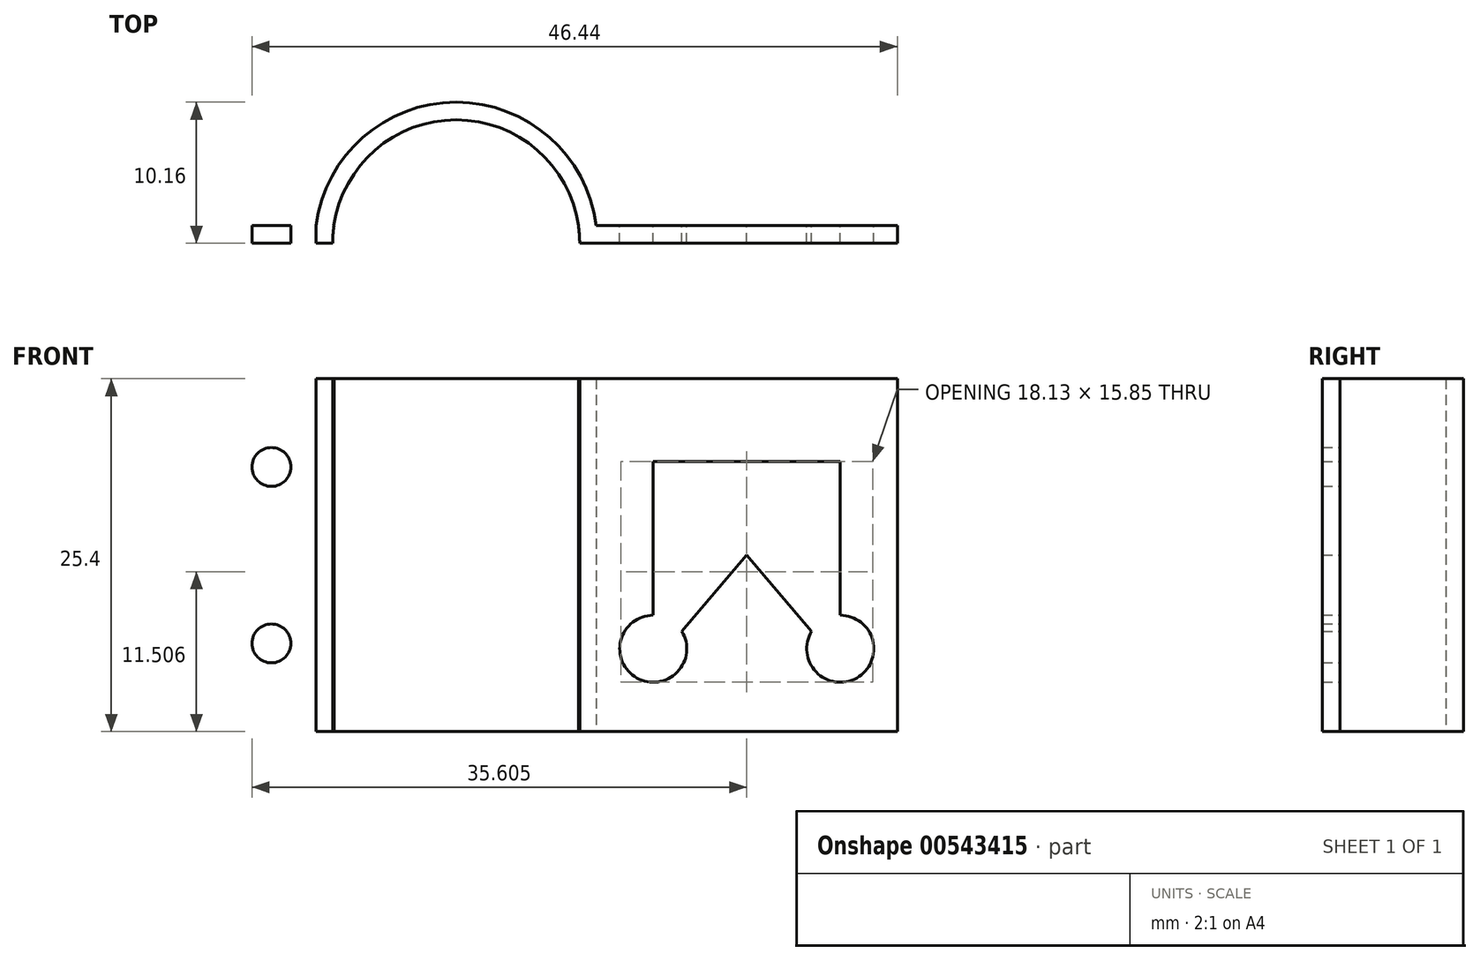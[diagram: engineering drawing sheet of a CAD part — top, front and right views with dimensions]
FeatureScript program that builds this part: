
annotation { "Feature Type Name" : "Feature", "Feature Type Description" : "" }
export const myFeature = defineFeature(function(context is Context, id is Id, definition is map)
    precondition{}
    {
        {
            var Q0;
            Q0=qCreatedBy(makeId("Top.planeOp"),FACE);
            var sketch = newSketch(context, id + "F0", { "sketchPlane" : qUnion([Q0])});
            skArc(sketch, "E0", {"start": v(8.8, 1.27) * mm, "mid": v(0, 8.9) * mm, "end": v(-8.8, 1.27) * mm});
            skArc(sketch, "E1", {"start": v(10.08, 1.27) * mm, "mid": v(0, 10.16) * mm, "end": v(-10.08, 1.27) * mm});
            skLineSegment(sketch, "E2", {"start": v(-10.16, 0) * mm, "end": v(-8.9, 0) * mm});
            skLineSegment(sketch, "E3.trimOffspring", {"start": v(8.9, 0) * mm, "end": v(10.16, 0) * mm});
            skLineSegment(sketch, "E4", {"start": v(-16.51, 0) * mm, "end": v(-8.89, 0) * mm});
            skLineSegment(sketch, "E5", {"start": v(-16.51, 1.27) * mm, "end": v(-10.08, 1.27) * mm});
            skLineSegment(sketch, "E6", {"start": v(-16.51, 1.27) * mm, "end": v(-16.51, 0) * mm});
            skLineSegment(sketch, "E7", {"start": v(31.75, 1.27) * mm, "end": v(31.75, 0) * mm});
            skPoint(sketch, "E8.start.orphan", {"position": v(-23.59, 0) * mm});
            skLineSegment(sketch, "E9.trimOffspring", {"start": v(-8.8, 1.27) * mm, "end": v(-8.8, 1.27) * mm});
            skLineSegment(sketch, "E10.trimOffspring", {"start": v(10.08, 1.27) * mm, "end": v(31.75, 1.27) * mm});
            skArc(sketch, "E11", {"start": v(8.9, 0) * mm, "mid": v(0, 8.86) * mm, "end": v(-8.9, 0) * mm});
            skLineSegment(sketch, "E12.trimOffspring", {"start": v(8.8, 1.27) * mm, "end": v(8.8, 1.27) * mm});
            skLineSegment(sketch, "E13.trimOffspring", {"start": v(8.9, 0) * mm, "end": v(31.75, 0) * mm});
            skSolve(sketch);
        }
        {
            var Q0;
            Q0=makeQuery(id+"F0.imprint","IMPRINT",FACE,{"disambiguationData":[TD([[makeQuery(id+"F0.imprint","IMPRINT",EDGE,{"derivedFrom":sQuery(id+"F0.wireOp",EDGE,"E0")}),-1.0]])]});
            extrude(context, id + "F1", {"entities" : qUnion([Q0]), "depth" : 25.4 * mm, "offsetDistance" : 25.4 * mm});
        }
        {
            var Q0;
            Q0=makeQuery(id+"F1.opExtrude","SWEPT_FACE",FACE,{"disambiguationData":[OSD([sQuery(id+"F0.wireOp",EDGE,"E5")])]});
            var sketch = newSketch(context, id + "F2", { "sketchPlane" : qUnion([Q0])});
            skLineSegment(sketch, "E14", {"start": v(13.3, 25.4) * mm, "end": v(13.3, 0) * mm});
            skPoint(sketch, "E15.orphan", {"position": v(10.08, 12.7) * mm});
            skPoint(sketch, "E16.orphan", {"position": v(16.51, 12.7) * mm});
            skCircle(sketch, "E17", {"center": v(13.3, 19.05) * mm, "radius": 1.4 * mm});
            skCircle(sketch, "E18", {"center": v(13.3, 12.7) * mm, "radius": 1.4 * mm});
            skCircle(sketch, "E19", {"center": v(13.3, 6.35) * mm, "radius": 1.4 * mm});
            skSolve(sketch);
        }
        {
            var Q0;
            Q0=makeQuery(id+"F1.opExtrude","SWEPT_FACE",FACE,{"disambiguationData":[OSD([sQuery(id+"F0.wireOp",EDGE,"E10.trimOffspring")])]});
            var sketch = newSketch(context, id + "F3", { "sketchPlane" : qUnion([Q0])});
            skLineSegment(sketch, "E20", {"start": v(-31.75, 25.4) * mm, "end": v(-10.08, 0) * mm});
            skLineSegment(sketch, "E21", {"start": v(-10.08, 25.4) * mm, "end": v(-31.75, 0) * mm});
            skLineSegment(sketch, "E22.bottom", {"start": v(-14.18, 19.43) * mm, "end": v(-27.65, 19.43) * mm});
            skLineSegment(sketch, "E22.top", {"start": v(-14.18, 5.97) * mm, "end": v(-27.65, 5.97) * mm});
            skLineSegment(sketch, "E22.left", {"start": v(-14.18, 19.43) * mm, "end": v(-14.18, 5.97) * mm});
            skLineSegment(sketch, "E22.right", {"start": v(-27.65, 19.43) * mm, "end": v(-27.65, 5.97) * mm});
            skPoint(sketch, "E22.middle", {"position": v(-20.92, 12.7) * mm});
            skCircle(sketch, "E23", {"center": v(-27.65, 19.43) * mm, "radius": 2.41 * mm});
            skCircle(sketch, "E24", {"center": v(-14.18, 19.43) * mm, "radius": 2.41 * mm});
            skCircle(sketch, "E25", {"center": v(-27.65, 5.97) * mm, "radius": 2.41 * mm});
            skCircle(sketch, "E26", {"center": v(-14.18, 5.97) * mm, "radius": 2.41 * mm});
            skSolve(sketch);
        }
        {
            var Q0;
            {var subQ0=sQuery(id+"F3.wireOp",EDGE,"E22.bottom");var subQ1=sQuery(id+"F3.wireOp",EDGE,"E20");var subQ2=makeQuery(id+"F3.imprint","INTERSECT",VERTEX,{"derivedFrom":[subQ1,subQ0]});Q0=makeQuery(id+"F3.imprint","IMPRINT",FACE,{"disambiguationData":[TD([[makeQuery(id+"F3.imprint","IMPRINT",EDGE,{"disambiguationData":[TD([[subQ2,-1.0]])],"derivedFrom":subQ1}),-1.0]])]});}
            var Q1;
            {var subQ0=sQuery(id+"F3.wireOp",EDGE,"E22.bottom");var subQ1=sQuery(id+"F3.wireOp",EDGE,"E20");var subQ2=makeQuery(id+"F3.imprint","INTERSECT",VERTEX,{"derivedFrom":[subQ1,subQ0]});Q1=makeQuery(id+"F3.imprint","IMPRINT",FACE,{"disambiguationData":[TD([[makeQuery(id+"F3.imprint","IMPRINT",EDGE,{"disambiguationData":[TD([[subQ2,-1.0]])],"derivedFrom":subQ1}),1.0]])]});}
            var Q2;
            {var subQ0=sQuery(id+"F3.wireOp",EDGE,"E23");var subQ1=sQuery(id+"F3.wireOp",EDGE,"E20");var subQ2=makeQuery(id+"F3.imprint","INTERSECT",VERTEX,{"disambiguationData":[OD(0.0)],"derivedFrom":[subQ1,subQ0]});Q2=makeQuery(id+"F3.imprint","IMPRINT",FACE,{"disambiguationData":[TD([[makeQuery(id+"F3.imprint","IMPRINT",EDGE,{"disambiguationData":[TD([[subQ2,-1.0]])],"derivedFrom":subQ1}),1.0]])]});}
            var Q3;
            {var subQ0=sQuery(id+"F3.wireOp",EDGE,"E23");var subQ1=sQuery(id+"F3.wireOp",EDGE,"E20");var subQ2=makeQuery(id+"F3.imprint","INTERSECT",VERTEX,{"disambiguationData":[OD(0.0)],"derivedFrom":[subQ1,subQ0]});Q3=makeQuery(id+"F3.imprint","IMPRINT",FACE,{"disambiguationData":[TD([[makeQuery(id+"F3.imprint","IMPRINT",EDGE,{"disambiguationData":[TD([[subQ2,-1.0]])],"derivedFrom":subQ1}),-1.0]])]});}
            var Q4;
            {var subQ0=sQuery(id+"F3.wireOp",EDGE,"E22.top");var subQ1=sQuery(id+"F3.wireOp",EDGE,"E21");var subQ2=makeQuery(id+"F3.imprint","INTERSECT",VERTEX,{"derivedFrom":[subQ1,subQ0]});Q4=makeQuery(id+"F3.imprint","IMPRINT",FACE,{"disambiguationData":[TD([[makeQuery(id+"F3.imprint","IMPRINT",EDGE,{"disambiguationData":[TD([[subQ2,-1.0]])],"derivedFrom":subQ1}),-1.0]])]});}
            var Q5;
            {var subQ0=sQuery(id+"F3.wireOp",EDGE,"E22.top");var subQ1=sQuery(id+"F3.wireOp",EDGE,"E21");var subQ2=makeQuery(id+"F3.imprint","INTERSECT",VERTEX,{"derivedFrom":[subQ1,subQ0]});Q5=makeQuery(id+"F3.imprint","IMPRINT",FACE,{"disambiguationData":[TD([[makeQuery(id+"F3.imprint","IMPRINT",EDGE,{"disambiguationData":[TD([[subQ2,-1.0]])],"derivedFrom":subQ1}),1.0]])]});}
            var Q6;
            {var subQ0=sQuery(id+"F3.wireOp",EDGE,"E25");var subQ1=sQuery(id+"F3.wireOp",EDGE,"E21");var subQ2=makeQuery(id+"F3.imprint","INTERSECT",VERTEX,{"disambiguationData":[OD(0.0)],"derivedFrom":[subQ1,subQ0]});Q6=makeQuery(id+"F3.imprint","IMPRINT",FACE,{"disambiguationData":[TD([[makeQuery(id+"F3.imprint","IMPRINT",EDGE,{"disambiguationData":[TD([[subQ2,-1.0]])],"derivedFrom":subQ1}),1.0]])]});}
            var Q7;
            {var subQ0=sQuery(id+"F3.wireOp",EDGE,"E25");var subQ1=sQuery(id+"F3.wireOp",EDGE,"E21");var subQ2=makeQuery(id+"F3.imprint","INTERSECT",VERTEX,{"disambiguationData":[OD(0.0)],"derivedFrom":[subQ1,subQ0]});Q7=makeQuery(id+"F3.imprint","IMPRINT",FACE,{"disambiguationData":[TD([[makeQuery(id+"F3.imprint","IMPRINT",EDGE,{"disambiguationData":[TD([[subQ2,-1.0]])],"derivedFrom":subQ1}),-1.0]])]});}
            var Q8;
            {var subQ0=sQuery(id+"F3.wireOp",EDGE,"E26");var subQ1=sQuery(id+"F3.wireOp",EDGE,"E20");var subQ2=makeQuery(id+"F3.imprint","INTERSECT",VERTEX,{"disambiguationData":[OD(0.0)],"derivedFrom":[subQ1,subQ0]});Q8=makeQuery(id+"F3.imprint","IMPRINT",FACE,{"disambiguationData":[TD([[makeQuery(id+"F3.imprint","IMPRINT",EDGE,{"disambiguationData":[TD([[subQ2,-1.0]])],"derivedFrom":subQ1}),-1.0]])]});}
            var Q9;
            {var subQ0=sQuery(id+"F3.wireOp",EDGE,"E22.top");var subQ1=sQuery(id+"F3.wireOp",EDGE,"E20");var subQ2=makeQuery(id+"F3.imprint","INTERSECT",VERTEX,{"derivedFrom":[subQ1,subQ0]});Q9=makeQuery(id+"F3.imprint","IMPRINT",FACE,{"disambiguationData":[TD([[makeQuery(id+"F3.imprint","IMPRINT",EDGE,{"disambiguationData":[TD([[subQ2,-1.0]])],"derivedFrom":subQ1}),-1.0]])]});}
            var Q10;
            {var subQ0=sQuery(id+"F3.wireOp",EDGE,"E22.top");var subQ1=sQuery(id+"F3.wireOp",EDGE,"E20");var subQ2=makeQuery(id+"F3.imprint","INTERSECT",VERTEX,{"derivedFrom":[subQ1,subQ0]});Q10=makeQuery(id+"F3.imprint","IMPRINT",FACE,{"disambiguationData":[TD([[makeQuery(id+"F3.imprint","IMPRINT",EDGE,{"disambiguationData":[TD([[subQ2,-1.0]])],"derivedFrom":subQ1}),1.0]])]});}
            var Q11;
            {var subQ0=sQuery(id+"F3.wireOp",EDGE,"E26");var subQ1=sQuery(id+"F3.wireOp",EDGE,"E20");var subQ2=makeQuery(id+"F3.imprint","INTERSECT",VERTEX,{"disambiguationData":[OD(0.0)],"derivedFrom":[subQ1,subQ0]});Q11=makeQuery(id+"F3.imprint","IMPRINT",FACE,{"disambiguationData":[TD([[makeQuery(id+"F3.imprint","IMPRINT",EDGE,{"disambiguationData":[TD([[subQ2,-1.0]])],"derivedFrom":subQ1}),1.0]])]});}
            var Q12;
            {var subQ0=sQuery(id+"F3.wireOp",EDGE,"E22.bottom");var subQ1=sQuery(id+"F3.wireOp",EDGE,"E21");var subQ2=makeQuery(id+"F3.imprint","INTERSECT",VERTEX,{"derivedFrom":[subQ1,subQ0]});Q12=makeQuery(id+"F3.imprint","IMPRINT",FACE,{"disambiguationData":[TD([[makeQuery(id+"F3.imprint","IMPRINT",EDGE,{"disambiguationData":[TD([[subQ2,-1.0]])],"derivedFrom":subQ1}),1.0]])]});}
            var Q13;
            {var subQ0=sQuery(id+"F3.wireOp",EDGE,"E22.bottom");var subQ1=sQuery(id+"F3.wireOp",EDGE,"E21");var subQ2=makeQuery(id+"F3.imprint","INTERSECT",VERTEX,{"derivedFrom":[subQ1,subQ0]});Q13=makeQuery(id+"F3.imprint","IMPRINT",FACE,{"disambiguationData":[TD([[makeQuery(id+"F3.imprint","IMPRINT",EDGE,{"disambiguationData":[TD([[subQ2,-1.0]])],"derivedFrom":subQ1}),-1.0]])]});}
            var Q14;
            {var subQ0=sQuery(id+"F3.wireOp",EDGE,"E24");var subQ1=sQuery(id+"F3.wireOp",EDGE,"E21");var subQ2=makeQuery(id+"F3.imprint","INTERSECT",VERTEX,{"disambiguationData":[OD(0.0)],"derivedFrom":[subQ1,subQ0]});Q14=makeQuery(id+"F3.imprint","IMPRINT",FACE,{"disambiguationData":[TD([[makeQuery(id+"F3.imprint","IMPRINT",EDGE,{"disambiguationData":[TD([[subQ2,-1.0]])],"derivedFrom":subQ1}),-1.0]])]});}
            var Q15;
            {var subQ0=sQuery(id+"F3.wireOp",EDGE,"E24");var subQ1=sQuery(id+"F3.wireOp",EDGE,"E21");var subQ2=makeQuery(id+"F3.imprint","INTERSECT",VERTEX,{"disambiguationData":[OD(0.0)],"derivedFrom":[subQ1,subQ0]});Q15=makeQuery(id+"F3.imprint","IMPRINT",FACE,{"disambiguationData":[TD([[makeQuery(id+"F3.imprint","IMPRINT",EDGE,{"disambiguationData":[TD([[subQ2,-1.0]])],"derivedFrom":subQ1}),1.0]])]});}
            var Q16;
            {var subQ0=sQuery(id+"F2.wireOp",EDGE,"E17");var subQ1=sQuery(id+"F2.wireOp",EDGE,"E14");var subQ2=makeQuery(id+"F2.imprint","INTERSECT",VERTEX,{"disambiguationData":[OD(0.0)],"derivedFrom":[subQ1,subQ0]});Q16=makeQuery(id+"F2.imprint","IMPRINT",FACE,{"disambiguationData":[TD([[makeQuery(id+"F2.imprint","IMPRINT",EDGE,{"disambiguationData":[TD([[subQ2,-1.0]])],"derivedFrom":subQ1}),-1.0]])]});}
            var Q17;
            {var subQ0=sQuery(id+"F2.wireOp",EDGE,"E17");var subQ1=sQuery(id+"F2.wireOp",EDGE,"E14");var subQ2=makeQuery(id+"F2.imprint","INTERSECT",VERTEX,{"disambiguationData":[OD(0.0)],"derivedFrom":[subQ1,subQ0]});Q17=makeQuery(id+"F2.imprint","IMPRINT",FACE,{"disambiguationData":[TD([[makeQuery(id+"F2.imprint","IMPRINT",EDGE,{"disambiguationData":[TD([[subQ2,-1.0]])],"derivedFrom":subQ1}),1.0]])]});}
            var Q18;
            {var subQ0=sQuery(id+"F2.wireOp",EDGE,"E18");var subQ1=sQuery(id+"F2.wireOp",EDGE,"E14");var subQ2=makeQuery(id+"F2.imprint","INTERSECT",VERTEX,{"disambiguationData":[OD(0.0)],"derivedFrom":[subQ1,subQ0]});Q18=makeQuery(id+"F2.imprint","IMPRINT",FACE,{"disambiguationData":[TD([[makeQuery(id+"F2.imprint","IMPRINT",EDGE,{"disambiguationData":[TD([[subQ2,-1.0]])],"derivedFrom":subQ1}),-1.0]])]});}
            var Q19;
            {var subQ0=sQuery(id+"F2.wireOp",EDGE,"E18");var subQ1=sQuery(id+"F2.wireOp",EDGE,"E14");var subQ2=makeQuery(id+"F2.imprint","INTERSECT",VERTEX,{"disambiguationData":[OD(0.0)],"derivedFrom":[subQ1,subQ0]});Q19=makeQuery(id+"F2.imprint","IMPRINT",FACE,{"disambiguationData":[TD([[makeQuery(id+"F2.imprint","IMPRINT",EDGE,{"disambiguationData":[TD([[subQ2,-1.0]])],"derivedFrom":subQ1}),1.0]])]});}
            var Q20;
            {var subQ0=sQuery(id+"F2.wireOp",EDGE,"E19");var subQ1=sQuery(id+"F2.wireOp",EDGE,"E14");var subQ2=makeQuery(id+"F2.imprint","INTERSECT",VERTEX,{"disambiguationData":[OD(0.0)],"derivedFrom":[subQ1,subQ0]});Q20=makeQuery(id+"F2.imprint","IMPRINT",FACE,{"disambiguationData":[TD([[makeQuery(id+"F2.imprint","IMPRINT",EDGE,{"disambiguationData":[TD([[subQ2,-1.0]])],"derivedFrom":subQ1}),-1.0]])]});}
            var Q21;
            {var subQ0=sQuery(id+"F2.wireOp",EDGE,"E19");var subQ1=sQuery(id+"F2.wireOp",EDGE,"E14");var subQ2=makeQuery(id+"F2.imprint","INTERSECT",VERTEX,{"disambiguationData":[OD(0.0)],"derivedFrom":[subQ1,subQ0]});Q21=makeQuery(id+"F2.imprint","IMPRINT",FACE,{"disambiguationData":[TD([[makeQuery(id+"F2.imprint","IMPRINT",EDGE,{"disambiguationData":[TD([[subQ2,-1.0]])],"derivedFrom":subQ1}),1.0]])]});}
            extrude(context, id + "F4", {"entities" : qUnion([Q0, Q1, Q2, Q3, Q4, Q5, Q6, Q7, Q8, Q9, Q10, Q11, Q12, Q13, Q14, Q15, Q16, Q17, Q18, Q19, Q20, Q21]), "operationType" : NewBodyOperationType.REMOVE, "oppositeDirection" : true, "depth" : 25.4 * mm, "offsetDistance" : 25.4 * mm});
        }
    });
